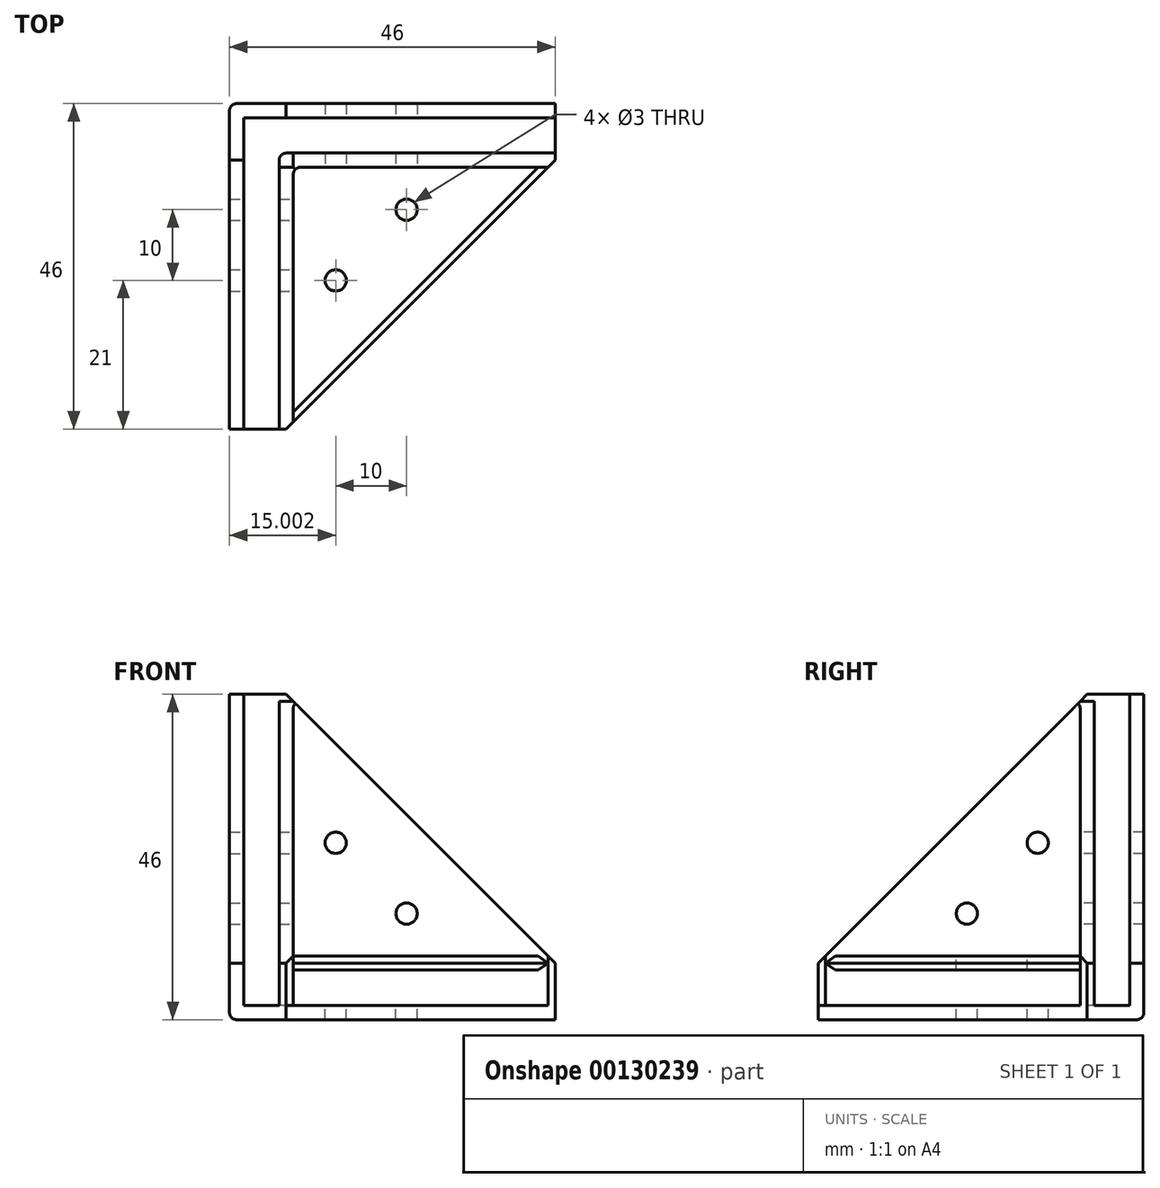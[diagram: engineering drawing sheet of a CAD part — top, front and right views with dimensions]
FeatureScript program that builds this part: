
annotation { "Feature Type Name" : "Feature", "Feature Type Description" : "" }
export const myFeature = defineFeature(function(context is Context, id is Id, definition is map)
    precondition{}
    {
        {
            var Q0;
            Q0=qCreatedBy(makeId("Front.planeOp"),FACE);
            var sketch = newSketch(context, id + "F0", { "sketchPlane" : qUnion([Q0])});
            skLineSegment(sketch, "E0", {"start": v(-20.48, 0) * mm, "end": v(24.52, 0) * mm});
            skLineSegment(sketch, "E1", {"start": v(24.52, 0) * mm, "end": v(24.52, 7) * mm});
            skLineSegment(sketch, "E2", {"start": v(24.52, 7) * mm, "end": v(-13.48, 45) * mm});
            skLineSegment(sketch, "E3", {"start": v(-13.48, 45) * mm, "end": v(-20.48, 45) * mm});
            skLineSegment(sketch, "E4", {"start": v(-20.48, 45) * mm, "end": v(-20.48, 0) * mm});
            skSolve(sketch);
        }
        {
            var Q0;
            Q0=makeQuery(id+"F0.imprint","IMPRINT",FACE,{"disambiguationData":[TD([[makeQuery(id+"F0.imprint","IMPRINT",EDGE,{"derivedFrom":sQuery(id+"F0.wireOp",EDGE,"E0")}),1.0]])]});
            extrude(context, id + "F1", {"entities" : qUnion([Q0]), "endBound" : BoundingType.SYMMETRIC, "depth" : 2 * mm});
        }
        {
            var Q0;
            Q0=makeQuery(id+"F1.opExtrude","CAP_VERTEX",VERTEX,{"disambiguationData":[OSD([sQuery(id+"F0.wireOp",EDGE,"E3"),sQuery(id+"F0.wireOp",EDGE,"E4")])],"isStart":true});
            var Q1;
            Q1=makeQuery(id+"F1.opExtrude","CAP_VERTEX",VERTEX,{"disambiguationData":[OSD([sQuery(id+"F0.wireOp",EDGE,"E3"),sQuery(id+"F0.wireOp",EDGE,"E4")])],"isStart":false});
            var Q2;
            Q2=makeQuery(id+"F1.opExtrude","CAP_VERTEX",VERTEX,{"disambiguationData":[OSD([sQuery(id+"F0.wireOp",EDGE,"E0"),sQuery(id+"F0.wireOp",EDGE,"E4")])],"isStart":false});
            cPlane(context, id + "F2", {"entities" : qUnion([Q0, Q1, Q2]), "cplaneType" : CPlaneType.THREE_POINT, "offset" : 25 * mm, "width" : 150 * mm, "height" : 150 * mm});
        }
        {
            var Q0;
            Q0=qCreatedBy(id+"F2.planeOp",FACE);
            var sketch = newSketch(context, id + "F3", { "sketchPlane" : qUnion([Q0])});
            skLineSegment(sketch, "E5", {"start": v(0, 0) * mm, "end": v(45, 0) * mm});
            skLineSegment(sketch, "E6", {"start": v(45, 0) * mm, "end": v(45, 7) * mm});
            skLineSegment(sketch, "E7", {"start": v(45, 7) * mm, "end": v(7, 45) * mm});
            skLineSegment(sketch, "E8", {"start": v(7, 45) * mm, "end": v(0, 45) * mm});
            skLineSegment(sketch, "E9", {"start": v(0, 45) * mm, "end": v(0, 0) * mm});
            skSolve(sketch);
        }
        {
            var Q0;
            Q0=makeQuery(id+"F3.imprint","IMPRINT",FACE,{"disambiguationData":[TD([[makeQuery(id+"F3.imprint","IMPRINT",EDGE,{"derivedFrom":sQuery(id+"F3.wireOp",EDGE,"E5")}),1.0]])]});
            extrude(context, id + "F4", {"entities" : qUnion([Q0]), "operationType" : NewBodyOperationType.ADD, "endBound" : BoundingType.SYMMETRIC, "depth" : 2 * mm});
        }
        {
            var Q0;
            Q0=qCreatedBy(makeId("Top.planeOp"),FACE);
            var sketch = newSketch(context, id + "F5", { "sketchPlane" : qUnion([Q0])});
            skLineSegment(sketch, "E10", {"start": v(-20.48, 0) * mm, "end": v(24.52, 0) * mm});
            skLineSegment(sketch, "E11", {"start": v(24.52, 0) * mm, "end": v(24.52, -7) * mm});
            skLineSegment(sketch, "E12", {"start": v(24.52, -7) * mm, "end": v(-13.48, -45) * mm});
            skLineSegment(sketch, "E13", {"start": v(-13.48, -45) * mm, "end": v(-20.48, -45) * mm});
            skLineSegment(sketch, "E14", {"start": v(-20.48, -45) * mm, "end": v(-20.48, 0) * mm});
            skSolve(sketch);
        }
        {
            var Q0;
            Q0=qSketchRegion(id+"F5",true);
            extrude(context, id + "F6", {"entities" : qUnion([Q0]), "operationType" : NewBodyOperationType.ADD, "endBound" : BoundingType.SYMMETRIC, "depth" : 2 * mm});
        }
        {
            var Q0;
            Q0=makeQuery(id+"F4.opExtrude","SWEPT_FACE",FACE,{"disambiguationData":[OSD([sQuery(id+"F3.wireOp",EDGE,"E9")])]});
            var Q1;
            Q1=makeQuery(id+"F4.boolean.opBoolean","INTERSECT",EDGE,{"derivedFrom":[makeQuery(id+"F1.opExtrude","SWEPT_FACE",FACE,{"disambiguationData":[OSD([sQuery(id+"F0.wireOp",EDGE,"E4")])]}),makeQuery(id+"F4.opExtrude","SWEPT_FACE",FACE,{"disambiguationData":[OSD([sQuery(id+"F3.wireOp",EDGE,"E9")])]})]});
            revolve(context, id + "F7", {"operationType" : NewBodyOperationType.ADD, "entities" : qUnion([Q0]), "axis" : qUnion([Q1]), "revolveType" : RevolveType.ONE_DIRECTION, "angle" : 90 * degree});
        }
        {
            var Q0;
            Q0=makeQuery(id+"F6.opExtrude","SWEPT_FACE",FACE,{"disambiguationData":[OSD([sQuery(id+"F5.wireOp",EDGE,"E10")])]});
            var Q1;
            Q1=makeQuery(id+"F6.boolean.opBoolean","INTERSECT",EDGE,{"derivedFrom":[makeQuery(id+"F4.boolean.opBoolean","MERGE",FACE,{"derivedFrom":[makeQuery(id+"F1.opExtrude","SWEPT_FACE",FACE,{"disambiguationData":[OSD([sQuery(id+"F0.wireOp",EDGE,"E0")])]}),makeQuery(id+"F4.opExtrude","SWEPT_FACE",FACE,{"disambiguationData":[OSD([sQuery(id+"F3.wireOp",EDGE,"E5")])]})]}),makeQuery(id+"F6.opExtrude","SWEPT_FACE",FACE,{"disambiguationData":[OSD([sQuery(id+"F5.wireOp",EDGE,"E10")])]})]});
            revolve(context, id + "F8", {"operationType" : NewBodyOperationType.ADD, "entities" : qUnion([Q0]), "axis" : qUnion([Q1]), "revolveType" : RevolveType.FULL});
        }
        {
            var Q0;
            {var subQ0=sQuery(id+"F5.wireOp",EDGE,"E14");Q0=makeQuery(id+"F8.boolean.opBoolean","MERGE",FACE,{"derivedFrom":[makeQuery(id+"F6.opExtrude","SWEPT_FACE",FACE,{"disambiguationData":[OSD([subQ0])]}),makeQuery(id+"F8.opRevolve","SWEPT_FACE",FACE,{"disambiguationData":[OSD([sQuery(id+"F5.wireOp",EDGE,"E10"),subQ0])]})]});}
            var Q1;
            {var subQ0=sQuery(id+"F5.wireOp",EDGE,"E14");var subQ1=sQuery(id+"F5.wireOp",EDGE,"E10");var subQ2=sQuery(id+"F3.wireOp",EDGE,"E9");var subQ3=sQuery(id+"F3.wireOp",EDGE,"E5");var subQ4=sQuery(id+"F3.wireOp",EDGE,"E6");var subQ5=makeQuery(id+"F4.opExtrude","SWEPT_FACE",FACE,{"disambiguationData":[OSD([subQ3])]});var subQ10=sQuery(id+"F0.wireOp",EDGE,"E0");var subQ11=makeQuery(id+"F1.opExtrude","SWEPT_FACE",FACE,{"disambiguationData":[OSD([subQ10])]});var subQ13=makeQuery(id+"F4.boolean.opBoolean","MERGE",FACE,{"derivedFrom":[subQ11,subQ5]});var subQ14=sQuery(id+"F0.wireOp",EDGE,"E1");Q1=makeQuery(id+"F8.boolean.opBoolean","INTERSECT",EDGE,{"derivedFrom":[makeQuery(id+"F7.boolean.opBoolean","MERGE",FACE,{"derivedFrom":[makeQuery(id+"F6.boolean.opBoolean","SPLIT",FACE,{"disambiguationData":[TD([makeQuery(id+"F1.opExtrude","SWEPT_FACE",FACE,{"disambiguationData":[OSD([subQ14])]})])],"derivedFrom":subQ13}),makeQuery(id+"F6.boolean.opBoolean","SPLIT",FACE,{"disambiguationData":[TD([makeQuery(id+"F4.opExtrude","SWEPT_FACE",FACE,{"disambiguationData":[OSD([subQ4])]})])],"derivedFrom":subQ13}),makeQuery(id+"F7.opRevolve","SWEPT_FACE",FACE,{"disambiguationData":[OSD([subQ3,subQ2])]})]}),makeQuery(id+"F8.opRevolve","SWEPT_FACE",FACE,{"disambiguationData":[OSD([subQ1,subQ0])]})]});}
            revolve(context, id + "F9", {"operationType" : NewBodyOperationType.ADD, "entities" : qUnion([Q0]), "axis" : qUnion([Q1]), "revolveType" : RevolveType.FULL});
        }
        {
            var Q0;
            Q0=makeQuery(id+"F4.opExtrude","CAP_FACE",FACE,{"disambiguationData":[OSD([sQuery(id+"F3.wireOp",EDGE,"E5"),sQuery(id+"F3.wireOp",EDGE,"E6"),sQuery(id+"F3.wireOp",EDGE,"E7"),sQuery(id+"F3.wireOp",EDGE,"E8"),sQuery(id+"F3.wireOp",EDGE,"E9")])],"isStart":true});
            var Q1;
            Q1=makeQuery(id+"F6.opExtrude","CAP_VERTEX",VERTEX,{"disambiguationData":[OSD([sQuery(id+"F5.wireOp",EDGE,"E12"),sQuery(id+"F5.wireOp",EDGE,"E13")])],"isStart":false});
            cPlane(context, id + "F10", {"entities" : qUnion([Q0, Q1]), "cplaneType" : CPlaneType.PLANE_POINT, "offset" : 25 * mm, "width" : 150 * mm, "height" : 150 * mm});
        }
        {
            var Q0;
            Q0=qCreatedBy(id+"F10.planeOp",FACE);
            var sketch = newSketch(context, id + "F11", { "sketchPlane" : qUnion([Q0])});
            skLineSegment(sketch, "E15", {"start": v(-45, 1) * mm, "end": v(-45, 7) * mm});
            skLineSegment(sketch, "E16", {"start": v(-7, 1) * mm, "end": v(-45, 1) * mm});
            skLineSegment(sketch, "E17", {"start": v(-7, 44) * mm, "end": v(-8, 44) * mm});
            skLineSegment(sketch, "E18", {"start": v(-8, 44) * mm, "end": v(-45, 7) * mm});
            skLineSegment(sketch, "E19", {"start": v(-7, 44) * mm, "end": v(-7, 1) * mm});
            skSolve(sketch);
        }
        {
            var Q0;
            Q0=makeQuery(id+"F1.opExtrude","CAP_FACE",FACE,{"disambiguationData":[OSD([sQuery(id+"F0.wireOp",EDGE,"E0"),sQuery(id+"F0.wireOp",EDGE,"E1"),sQuery(id+"F0.wireOp",EDGE,"E2"),sQuery(id+"F0.wireOp",EDGE,"E3"),sQuery(id+"F0.wireOp",EDGE,"E4")])],"isStart":false});
            var Q1;
            Q1=makeQuery(id+"F6.opExtrude","CAP_VERTEX",VERTEX,{"disambiguationData":[OSD([sQuery(id+"F5.wireOp",EDGE,"E11"),sQuery(id+"F5.wireOp",EDGE,"E12")])],"isStart":false});
            cPlane(context, id + "F12", {"entities" : qUnion([Q0, Q1]), "cplaneType" : CPlaneType.PLANE_POINT, "offset" : 25 * mm, "width" : 150 * mm, "height" : 150 * mm});
        }
        {
            var Q0;
            Q0=qCreatedBy(id+"F12.planeOp",FACE);
            var sketch = newSketch(context, id + "F13", { "sketchPlane" : qUnion([Q0])});
            skLineSegment(sketch, "E20", {"start": v(24.52, 1) * mm, "end": v(-13.48, 1) * mm});
            skLineSegment(sketch, "E21", {"start": v(24.52, 7) * mm, "end": v(24.52, 1) * mm});
            skLineSegment(sketch, "E22", {"start": v(-13.48, 44) * mm, "end": v(-12.48, 44) * mm});
            skLineSegment(sketch, "E23", {"start": v(-12.48, 44) * mm, "end": v(24.52, 7) * mm});
            skLineSegment(sketch, "E24", {"start": v(-13.48, 44) * mm, "end": v(-13.48, 1) * mm});
            skSolve(sketch);
        }
        {
            var Q0;
            Q0=qSketchRegion(id+"F11",true);
            extrude(context, id + "F14", {"entities" : qUnion([Q0]), "operationType" : NewBodyOperationType.ADD, "endBound" : BoundingType.SYMMETRIC, "depth" : 2 * mm});
        }
        {
            var Q0;
            Q0=makeQuery(id+"F13.imprint","IMPRINT",FACE,{"disambiguationData":[TD([[makeQuery(id+"F13.imprint","IMPRINT",EDGE,{"derivedFrom":sQuery(id+"F13.wireOp",EDGE,"E20")}),-1.0]])]});
            extrude(context, id + "F15", {"entities" : qUnion([Q0]), "operationType" : NewBodyOperationType.ADD, "endBound" : BoundingType.SYMMETRIC, "depth" : 2 * mm});
        }
        {
            var Q0;
            Q0=makeQuery(id+"F15.opExtrude","SWEPT_FACE",FACE,{"disambiguationData":[OSD([sQuery(id+"F13.wireOp",EDGE,"E24")])]});
            var Q1;
            Q1=makeQuery(id+"F15.boolean.opBoolean","INTERSECT",EDGE,{"derivedFrom":[makeQuery(id+"F14.opExtrude","SWEPT_FACE",FACE,{"disambiguationData":[OSD([sQuery(id+"F11.wireOp",EDGE,"E19")])]}),makeQuery(id+"F15.opExtrude","SWEPT_FACE",FACE,{"disambiguationData":[OSD([sQuery(id+"F13.wireOp",EDGE,"E24")])]})]});
            revolve(context, id + "F16", {"operationType" : NewBodyOperationType.ADD, "entities" : qUnion([Q0]), "axis" : qUnion([Q1]), "revolveType" : RevolveType.FULL});
        }
        {
            var Q0;
            Q0=makeQuery(id+"F14.opExtrude","CAP_EDGE",EDGE,{"disambiguationData":[OSD([sQuery(id+"F11.wireOp",EDGE,"E15")])],"isStart":false});
            var Q1;
            Q1=makeQuery(id+"F15.opExtrude","CAP_EDGE",EDGE,{"disambiguationData":[OSD([sQuery(id+"F13.wireOp",EDGE,"E21")])],"isStart":false});
            chamfer(context, id + "F17", {"entities" : qUnion([Q0, Q1]), "chamferType" : ChamferType.OFFSET_ANGLE, "width" : 1 * mm, "oppositeDirection" : true, "angle" : 45 * degree});
        }
        {
            var Q0;
            Q0=makeQuery(id+"F15.boolean.opBoolean","INTERSECT",EDGE,{"derivedFrom":[makeQuery(id+"F14.opExtrude","CAP_FACE",FACE,{"disambiguationData":[OSD([sQuery(id+"F11.wireOp",EDGE,"E15"),sQuery(id+"F11.wireOp",EDGE,"E16"),sQuery(id+"F11.wireOp",EDGE,"E17"),sQuery(id+"F11.wireOp",EDGE,"E18"),sQuery(id+"F11.wireOp",EDGE,"E19")])],"isStart":false}),makeQuery(id+"F15.opExtrude","CAP_FACE",FACE,{"disambiguationData":[OSD([sQuery(id+"F13.wireOp",EDGE,"E20"),sQuery(id+"F13.wireOp",EDGE,"E21"),sQuery(id+"F13.wireOp",EDGE,"E22"),sQuery(id+"F13.wireOp",EDGE,"E23"),sQuery(id+"F13.wireOp",EDGE,"E24")])],"isStart":false})]});
            fillet(context, id + "F18", {"entities" : qUnion([Q0]), "radius" : 1 * mm, "tangentPropagation" : true, "allowEdgeOverflow" : false});
        }
        {
            var Q0;
            Q0=makeQuery(id+"F4.opExtrude","CAP_VERTEX",VERTEX,{"disambiguationData":[OSD([sQuery(id+"F3.wireOp",EDGE,"E6"),sQuery(id+"F3.wireOp",EDGE,"E7")])],"isStart":false});
            var Q1;
            {var subQ0=sQuery(id+"F11.wireOp",EDGE,"E15");Q1=makeQuery(id+"F17.opChamfer","BLEND_VERTEX",VERTEX,{"blendedFrom":[makeQuery(id+"F14.opExtrude","CAP_EDGE",EDGE,{"disambiguationData":[OSD([subQ0])],"isStart":false}),makeQuery(id+"F14.opExtrude","SWEPT_FACE",FACE,{"disambiguationData":[OSD([subQ0])]}),makeQuery(id+"F14.opExtrude","SWEPT_FACE",FACE,{"disambiguationData":[OSD([sQuery(id+"F11.wireOp",EDGE,"E18")])]})],"blendedInto":[makeQuery(id+"F14.opExtrude","SWEPT_FACE",FACE,{"disambiguationData":[OSD([subQ0])]}),makeQuery(id+"F14.opExtrude","SWEPT_FACE",FACE,{"disambiguationData":[OSD([sQuery(id+"F11.wireOp",EDGE,"E18")])]})]});}
            var Q2;
            Q2=makeQuery(id+"F1.opExtrude","CAP_VERTEX",VERTEX,{"disambiguationData":[OSD([sQuery(id+"F0.wireOp",EDGE,"E1"),sQuery(id+"F0.wireOp",EDGE,"E2")])],"isStart":false});
            cPlane(context, id + "F19", {"entities" : qUnion([Q0, Q1, Q2]), "cplaneType" : CPlaneType.THREE_POINT, "offset" : 25 * mm, "width" : 150 * mm, "height" : 150 * mm});
        }
        {
            var Q0;
            Q0=qCreatedBy(id+"F19.planeOp",FACE);
            var sketch = newSketch(context, id + "F20", { "sketchPlane" : qUnion([Q0])});
            skLineSegment(sketch, "E25", {"start": v(-13.48, 45) * mm, "end": v(-13.48, 7) * mm});
            skLineSegment(sketch, "E26", {"start": v(-13.48, 7) * mm, "end": v(24.52, 7) * mm});
            skLineSegment(sketch, "E27", {"start": v(24.52, 7) * mm, "end": v(-13.48, 45) * mm});
            skSolve(sketch);
        }
        {
            var Q0;
            Q0=makeQuery(id+"F20.imprint","IMPRINT",FACE,{"disambiguationData":[TD([[makeQuery(id+"F20.imprint","IMPRINT",EDGE,{"derivedFrom":sQuery(id+"F20.wireOp",EDGE,"E25")}),1.0]])]});
            extrude(context, id + "F21", {"entities" : qUnion([Q0]), "operationType" : NewBodyOperationType.ADD, "endBound" : BoundingType.SYMMETRIC, "depth" : 2 * mm, "hasDraft" : true, "draftAngle" : 45 * degree, "draftPullDirection" : true});
        }
        {
            var Q0;
            {var subQ0=sQuery(id+"F13.wireOp",EDGE,"E24");var subQ1=sQuery(id+"F13.wireOp",EDGE,"E23");var subQ2=sQuery(id+"F13.wireOp",EDGE,"E22");var subQ3=sQuery(id+"F13.wireOp",EDGE,"E21");var subQ4=sQuery(id+"F13.wireOp",EDGE,"E20");var subQ6=makeQuery(id+"F15.opExtrude","CAP_FACE",FACE,{"disambiguationData":[OSD([subQ4,subQ3,subQ2,subQ1,subQ0])],"isStart":false});Q0=makeQuery(id+"F21.boolean.opBoolean","SPLIT",FACE,{"disambiguationData":[TD([makeQuery(id+"F15.opExtrude","SWEPT_FACE",FACE,{"disambiguationData":[OSD([subQ1])]})])],"derivedFrom":subQ6});}
            var sketch = newSketch(context, id + "F22", { "sketchPlane" : qUnion([Q0])});
            skCircle(sketch, "E28", {"center": v(-6.48, 24) * mm, "radius": 1.5 * mm});
            skCircle(sketch, "E29", {"center": v(3.52, 14) * mm, "radius": 1.5 * mm});
            skSolve(sketch);
        }
        {
            var Q0;
            Q0=makeQuery(id+"F22.imprint","IMPRINT",FACE,{"disambiguationData":[TD([[makeQuery(id+"F22.imprint","IMPRINT",EDGE,{"derivedFrom":sQuery(id+"F22.wireOp",EDGE,"E28")}),1.0]])]});
            var Q1;
            Q1=makeQuery(id+"F22.imprint","IMPRINT",FACE,{"disambiguationData":[TD([[makeQuery(id+"F22.imprint","IMPRINT",EDGE,{"derivedFrom":sQuery(id+"F22.wireOp",EDGE,"E29")}),1.0]])]});
            extrude(context, id + "F23", {"entities" : qUnion([Q0, Q1]), "operationType" : NewBodyOperationType.REMOVE, "endBound" : BoundingType.THROUGH_ALL, "oppositeDirection" : true, "depth" : 25 * mm});
        }
        {
            var Q0;
            Q0=makeQuery(id+"F14.opExtrude","CAP_FACE",FACE,{"disambiguationData":[OSD([sQuery(id+"F11.wireOp",EDGE,"E15"),sQuery(id+"F11.wireOp",EDGE,"E16"),sQuery(id+"F11.wireOp",EDGE,"E17"),sQuery(id+"F11.wireOp",EDGE,"E18"),sQuery(id+"F11.wireOp",EDGE,"E19")])],"isStart":false});
            var sketch = newSketch(context, id + "F24", { "sketchPlane" : qUnion([Q0])});
            skCircle(sketch, "E30", {"center": v(-14, 24) * mm, "radius": 1.5 * mm});
            skCircle(sketch, "E31", {"center": v(-24, 14) * mm, "radius": 1.5 * mm});
            skSolve(sketch);
        }
        {
            var Q0;
            Q0=makeQuery(id+"F24.imprint","IMPRINT",FACE,{"disambiguationData":[TD([[makeQuery(id+"F24.imprint","IMPRINT",EDGE,{"derivedFrom":sQuery(id+"F24.wireOp",EDGE,"E30")}),1.0]])]});
            var Q1;
            Q1=makeQuery(id+"F24.imprint","IMPRINT",FACE,{"disambiguationData":[TD([[makeQuery(id+"F24.imprint","IMPRINT",EDGE,{"derivedFrom":sQuery(id+"F24.wireOp",EDGE,"E31")}),1.0]])]});
            extrude(context, id + "F25", {"entities" : qUnion([Q0, Q1]), "operationType" : NewBodyOperationType.REMOVE, "endBound" : BoundingType.THROUGH_ALL, "oppositeDirection" : true, "depth" : 25 * mm});
        }
        {
            var Q0;
            Q0=makeQuery(id+"F21.opExtrude","CAP_FACE",FACE,{"disambiguationData":[OSD([sQuery(id+"F20.wireOp",EDGE,"E25"),sQuery(id+"F20.wireOp",EDGE,"E26"),sQuery(id+"F20.wireOp",EDGE,"E27")])],"isStart":true});
            var sketch = newSketch(context, id + "F26", { "sketchPlane" : qUnion([Q0])});
            skCircle(sketch, "E32", {"center": v(-6.48, -24) * mm, "radius": 1.5 * mm});
            skCircle(sketch, "E33", {"center": v(3.52, -14) * mm, "radius": 1.5 * mm});
            skSolve(sketch);
        }
        {
            var Q0;
            Q0=makeQuery(id+"F26.imprint","IMPRINT",FACE,{"disambiguationData":[TD([[makeQuery(id+"F26.imprint","IMPRINT",EDGE,{"derivedFrom":sQuery(id+"F26.wireOp",EDGE,"E33")}),1.0]])]});
            var Q1;
            Q1=makeQuery(id+"F26.imprint","IMPRINT",FACE,{"disambiguationData":[TD([[makeQuery(id+"F26.imprint","IMPRINT",EDGE,{"derivedFrom":sQuery(id+"F26.wireOp",EDGE,"E32")}),1.0]])]});
            extrude(context, id + "F27", {"entities" : qUnion([Q0, Q1]), "operationType" : NewBodyOperationType.REMOVE, "endBound" : BoundingType.THROUGH_ALL, "oppositeDirection" : true, "depth" : 25 * mm});
        }
    });
